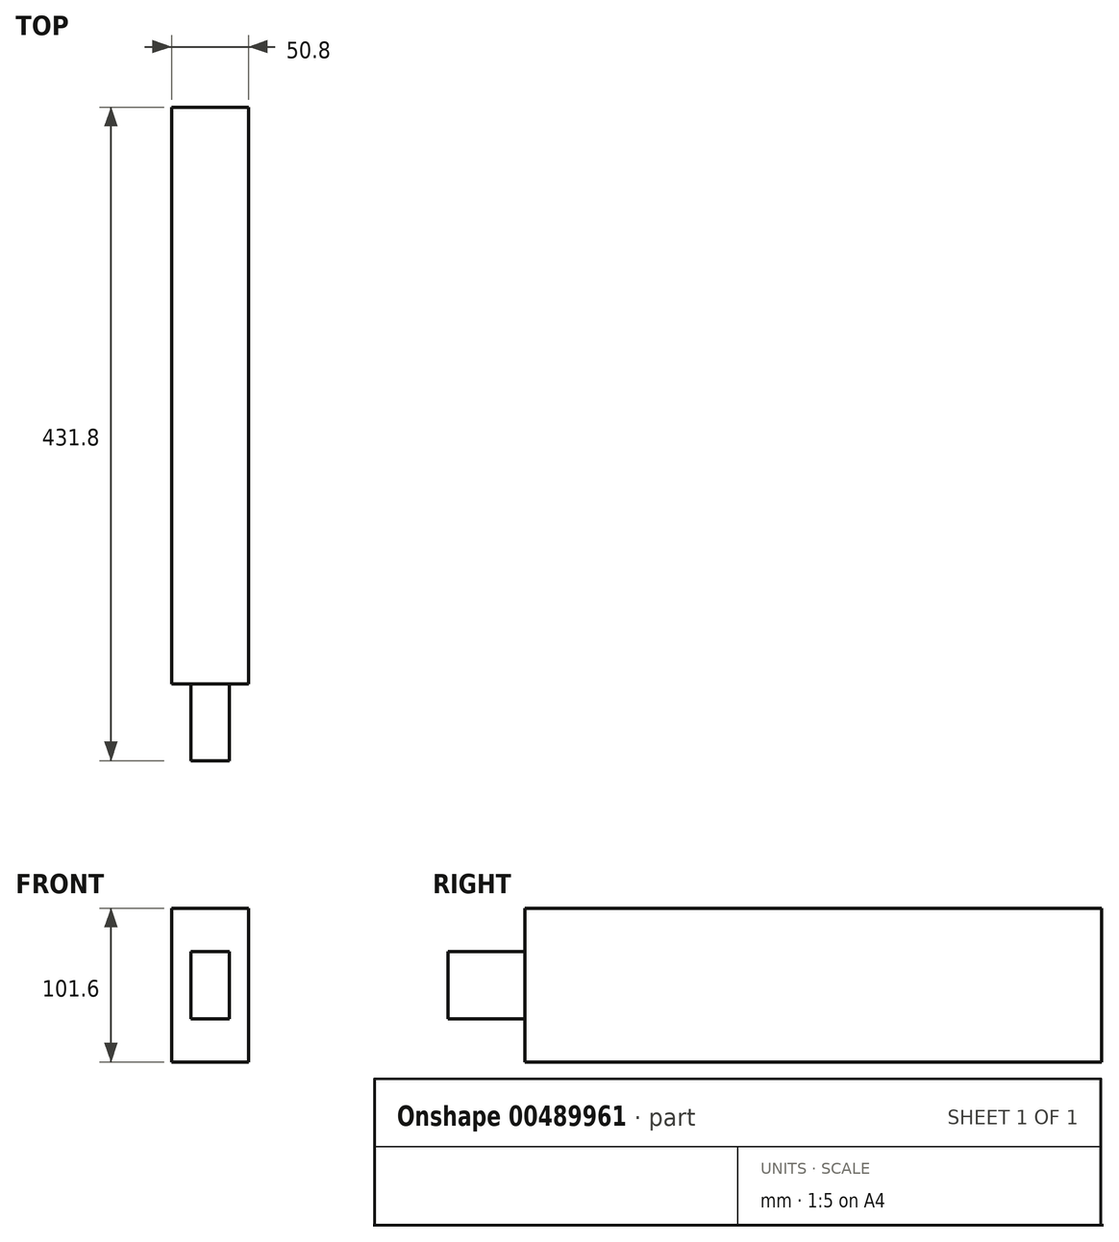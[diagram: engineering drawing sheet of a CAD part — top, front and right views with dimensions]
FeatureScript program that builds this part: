
annotation { "Feature Type Name" : "Feature", "Feature Type Description" : "" }
export const myFeature = defineFeature(function(context is Context, id is Id, definition is map)
    precondition{}
    {
        {
            var Q0;
            Q0=qCreatedBy(makeId("Front.planeOp"),FACE);
            var sketch = newSketch(context, id + "F0", { "sketchPlane" : qUnion([Q0])});
            skLineSegment(sketch, "E0.bottom", {"start": v(-25.4, -50.8) * mm, "end": v(25.4, -50.8) * mm});
            skLineSegment(sketch, "E0.top", {"start": v(-25.4, 50.8) * mm, "end": v(25.4, 50.8) * mm});
            skLineSegment(sketch, "E0.left", {"start": v(-25.4, -50.8) * mm, "end": v(-25.4, 50.8) * mm});
            skLineSegment(sketch, "E0.right", {"start": v(25.4, -50.8) * mm, "end": v(25.4, 50.8) * mm});
            skPoint(sketch, "E0.middle", {"position": v(0, 0) * mm});
            skSolve(sketch);
        }
        {
            var Q0;
            Q0 = qSketchRegion(id + "F0", true);
            extrude(context, id + "F1", {"entities" : qUnion([Q0]), "endBound" : BoundingType.SYMMETRIC, "depth" : 431.8 * mm});
        }
        {
            var Q0;
            Q0=makeQuery(id+"F1.opExtrude","CAP_FACE",FACE,{"disambiguationData":[OSD([sQuery(id+"F0.wireOp",EDGE,"E0.bottom"),sQuery(id+"F0.wireOp",EDGE,"E0.top"),sQuery(id+"F0.wireOp",EDGE,"E0.left"),sQuery(id+"F0.wireOp",EDGE,"E0.right")])],"isStart":false});
            var sketch = newSketch(context, id + "F2", { "sketchPlane" : qUnion([Q0])});
            skLineSegment(sketch, "E1.bottom", {"start": v(-12.7, 22.23) * mm, "end": v(12.7, 22.23) * mm});
            skLineSegment(sketch, "E1.top", {"start": v(-12.7, -22.23) * mm, "end": v(12.7, -22.23) * mm});
            skLineSegment(sketch, "E1.left", {"start": v(-12.7, 22.23) * mm, "end": v(-12.7, -22.23) * mm});
            skLineSegment(sketch, "E1.right", {"start": v(12.7, 22.23) * mm, "end": v(12.7, -22.23) * mm});
            skPoint(sketch, "E1.middle", {"position": v(0, 0) * mm});
            skLineSegment(sketch, "E2.bottom", {"start": v(-25.4, 50.8) * mm, "end": v(25.4, 50.8) * mm});
            skLineSegment(sketch, "E2.top", {"start": v(-25.4, -50.8) * mm, "end": v(25.4, -50.8) * mm});
            skLineSegment(sketch, "E2.left", {"start": v(-25.4, 50.8) * mm, "end": v(-25.4, -50.8) * mm});
            skLineSegment(sketch, "E2.right", {"start": v(25.4, 50.8) * mm, "end": v(25.4, -50.8) * mm});
            skSolve(sketch);
        }
        {
            var Q0;
            Q0=makeQuery(id+"F2.imprint","IMPRINT",FACE,{"disambiguationData":[TD([[makeQuery(id+"F2.imprint","IMPRINT",EDGE,{"derivedFrom":sQuery(id+"F2.wireOp",EDGE,"E1.bottom")}),1.0]])]});
            extrude(context, id + "F3", {"entities" : qUnion([Q0]), "operationType" : NewBodyOperationType.REMOVE, "oppositeDirection" : true, "depth" : 50.8 * mm});
        }
    });
